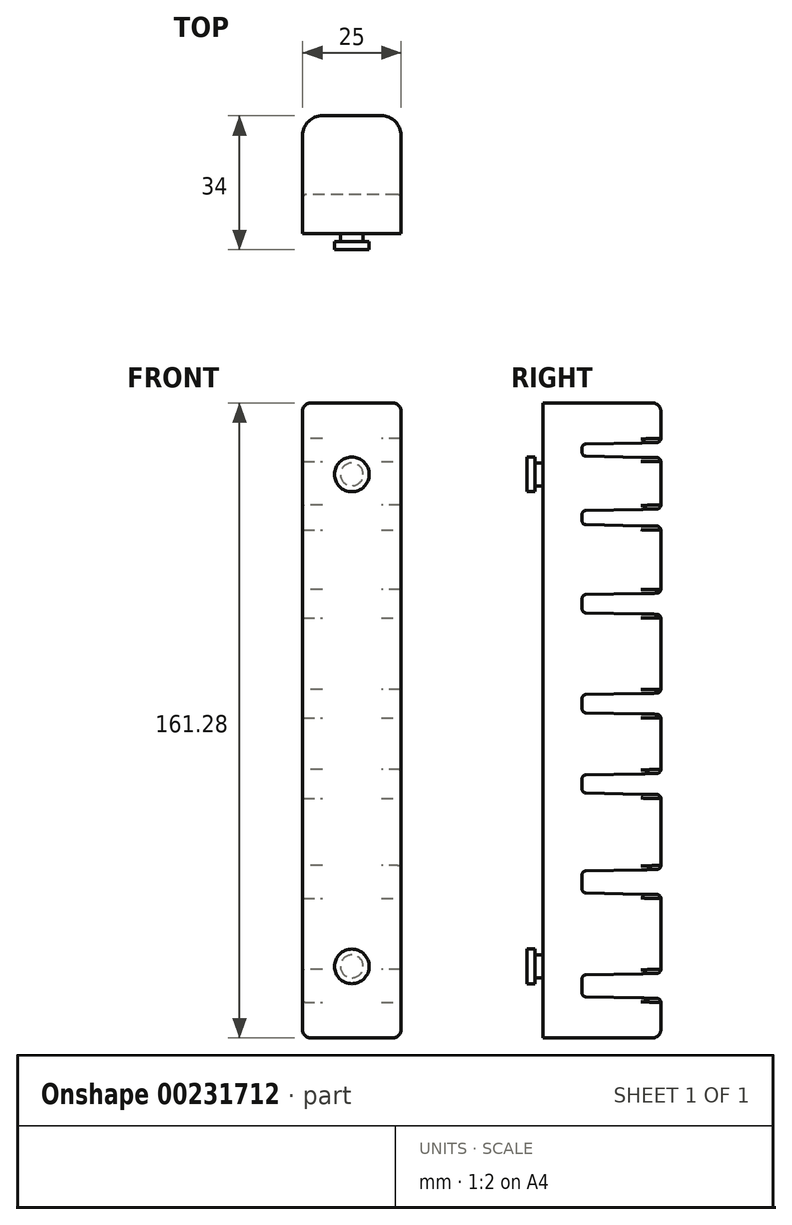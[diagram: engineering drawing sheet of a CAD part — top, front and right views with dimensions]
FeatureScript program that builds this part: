
annotation { "Feature Type Name" : "Feature", "Feature Type Description" : "" }
export const myFeature = defineFeature(function(context is Context, id is Id, definition is map)
    precondition{}
    {
        {
            var Q0;
            Q0=qCreatedBy(makeId("Right.planeOp"),FACE);
            var sketch = newSketch(context, id + "F0", { "sketchPlane" : qUnion([Q0])});
            skLineSegment(sketch, "E0", {"start": v(0, 16.4) * mm, "end": v(-20, 16) * mm});
            skLineSegment(sketch, "E1", {"start": v(-20, 16) * mm, "end": v(-20, 10.4) * mm});
            skLineSegment(sketch, "E2", {"start": v(-20, 10.4) * mm, "end": v(0, 10) * mm});
            skLineSegment(sketch, "E3", {"start": v(-20, 13.2) * mm, "end": v(0, 13.2) * mm, "construction": true});
            skLineSegment(sketch, "E4", {"start": v(-10, 16.2) * mm, "end": v(-9.88, 10.2) * mm, "construction": true});
            skLineSegment(sketch, "E5", {"start": v(0, 42.8) * mm, "end": v(-20, 42.4) * mm});
            skLineSegment(sketch, "E6", {"start": v(-20, 42.4) * mm, "end": v(-20, 36.8) * mm});
            skLineSegment(sketch, "E7", {"start": v(-20, 36.8) * mm, "end": v(0, 36.4) * mm});
            skLineSegment(sketch, "E8", {"start": v(-20, 39.6) * mm, "end": v(0, 39.6) * mm, "construction": true});
            skLineSegment(sketch, "E9", {"start": v(-10, 42.6) * mm, "end": v(-9.88, 36.6) * mm, "construction": true});
            skLineSegment(sketch, "E10", {"start": v(0, 67.19) * mm, "end": v(-20, 66.79) * mm});
            skLineSegment(sketch, "E11", {"start": v(-20, 66.79) * mm, "end": v(-20, 62.2) * mm});
            skLineSegment(sketch, "E12", {"start": v(-20, 62.2) * mm, "end": v(0, 61.8) * mm});
            skLineSegment(sketch, "E13", {"start": v(-20, 64.5) * mm, "end": v(0, 64.5) * mm, "construction": true});
            skLineSegment(sketch, "E14", {"start": v(-10, 66.99) * mm, "end": v(-9.9, 62) * mm, "construction": true});
            skLineSegment(sketch, "E15", {"start": v(0, 87.59) * mm, "end": v(-20, 87.19) * mm});
            skLineSegment(sketch, "E16", {"start": v(-20, 87.19) * mm, "end": v(-20, 82.59) * mm});
            skLineSegment(sketch, "E17", {"start": v(-20, 82.59) * mm, "end": v(0, 82.19) * mm});
            skLineSegment(sketch, "E18", {"start": v(-20, 84.89) * mm, "end": v(0, 84.89) * mm, "construction": true});
            skLineSegment(sketch, "E19", {"start": v(-10, 87.39) * mm, "end": v(-9.9, 82.39) * mm, "construction": true});
            skLineSegment(sketch, "E20", {"start": v(0, 112.98) * mm, "end": v(-20, 112.58) * mm});
            skLineSegment(sketch, "E21", {"start": v(-20, 112.58) * mm, "end": v(-20, 107.99) * mm});
            skLineSegment(sketch, "E22", {"start": v(-20, 107.99) * mm, "end": v(0, 107.59) * mm});
            skLineSegment(sketch, "E23", {"start": v(-20, 110.29) * mm, "end": v(0, 110.29) * mm, "construction": true});
            skLineSegment(sketch, "E24", {"start": v(-10, 112.78) * mm, "end": v(-9.9, 107.78) * mm, "construction": true});
            skLineSegment(sketch, "E25", {"start": v(0, 134.38) * mm, "end": v(-20, 133.98) * mm});
            skLineSegment(sketch, "E26", {"start": v(-20, 133.98) * mm, "end": v(-20, 130.38) * mm});
            skLineSegment(sketch, "E27", {"start": v(-20, 130.38) * mm, "end": v(0, 129.98) * mm});
            skLineSegment(sketch, "E28", {"start": v(-20, 132.18) * mm, "end": v(0, 132.18) * mm, "construction": true});
            skLineSegment(sketch, "E29", {"start": v(-10, 134.18) * mm, "end": v(-9.92, 130.18) * mm, "construction": true});
            skLineSegment(sketch, "E30", {"start": v(0, 151.28) * mm, "end": v(-20, 150.88) * mm});
            skLineSegment(sketch, "E31", {"start": v(-20, 150.88) * mm, "end": v(-20, 147.78) * mm});
            skLineSegment(sketch, "E32", {"start": v(-20, 147.78) * mm, "end": v(0, 147.38) * mm});
            skLineSegment(sketch, "E33", {"start": v(-20, 149.33) * mm, "end": v(0, 149.33) * mm, "construction": true});
            skLineSegment(sketch, "E34", {"start": v(-10, 151.08) * mm, "end": v(-9.93, 147.58) * mm, "construction": true});
            skLineSegment(sketch, "E35", {"start": v(-30, 0) * mm, "end": v(0, 0) * mm});
            skLineSegment(sketch, "E36", {"start": v(0, 0) * mm, "end": v(0, 10) * mm});
            skLineSegment(sketch, "E37", {"start": v(0, 16.4) * mm, "end": v(0, 36.4) * mm});
            skLineSegment(sketch, "E38", {"start": v(0, 42.8) * mm, "end": v(0, 61.8) * mm});
            skLineSegment(sketch, "E39", {"start": v(0, 67.19) * mm, "end": v(0, 82.19) * mm});
            skLineSegment(sketch, "E40", {"start": v(0, 87.59) * mm, "end": v(0, 107.59) * mm});
            skLineSegment(sketch, "E41", {"start": v(0, 112.98) * mm, "end": v(0, 129.98) * mm});
            skLineSegment(sketch, "E42", {"start": v(0, 134.38) * mm, "end": v(0, 147.38) * mm});
            skLineSegment(sketch, "E43", {"start": v(0, 161.28) * mm, "end": v(-30, 161.28) * mm});
            skLineSegment(sketch, "E44", {"start": v(-30, 161.28) * mm, "end": v(-30, 0) * mm});
            skLineSegment(sketch, "E45", {"start": v(0, 151.28) * mm, "end": v(0, 161.28) * mm});
            skSolve(sketch);
        }
        {
            var Q0;
            Q0=makeQuery(id+"F0.imprint","IMPRINT",FACE,{"disambiguationData":[TD([[makeQuery(id+"F0.imprint","IMPRINT",EDGE,{"derivedFrom":sQuery(id+"F0.wireOp",EDGE,"E0")}),-1.0]])]});
            extrude(context, id + "F1", {"entities" : qUnion([Q0]), "depth" : 25 * mm});
        }
        {
            var Q0;
            Q0=makeQuery(id+"F1.opExtrude","SWEPT_FACE",FACE,{"disambiguationData":[OSD([sQuery(id+"F0.wireOp",EDGE,"E44")])]});
            var sketch = newSketch(context, id + "F2", { "sketchPlane" : qUnion([Q0])});
            skLineSegment(sketch, "E46", {"start": v(12.5, 161.28) * mm, "end": v(12.5, 0) * mm, "construction": true});
            skCircle(sketch, "E47", {"center": v(12.5, 143.14) * mm, "radius": 2.9 * mm});
            skCircle(sketch, "E48", {"center": v(12.5, 18.14) * mm, "radius": 2.9 * mm});
            skLineSegment(sketch, "E49", {"start": v(25, 80.64) * mm, "end": v(0, 80.64) * mm, "construction": true});
            skSolve(sketch);
        }
        {
            var Q0;
            Q0 = qSketchRegion(id + "F2", true);
            extrude(context, id + "F3", {"entities" : qUnion([Q0]), "operationType" : NewBodyOperationType.ADD, "depth" : 2 * mm});
        }
        {
            var Q0;
            Q0=makeQuery(id+"F3.opExtrude","CAP_FACE",FACE,{"disambiguationData":[OSD([sQuery(id+"F2.wireOp",EDGE,"E47")])],"isStart":false});
            var sketch = newSketch(context, id + "F4", { "sketchPlane" : qUnion([Q0])});
            skCircle(sketch, "E50.0", {"center": v(12.5, 18.14) * mm, "radius": 2.9 * mm, "construction": true});
            skCircle(sketch, "E51", {"center": v(12.5, 143.14) * mm, "radius": 4.4 * mm});
            skCircle(sketch, "E52", {"center": v(12.5, 18.14) * mm, "radius": 4.4 * mm});
            skSolve(sketch);
        }
        {
            var Q0;
            Q0 = qSketchRegion(id + "F4", true);
            extrude(context, id + "F5", {"entities" : qUnion([Q0]), "operationType" : NewBodyOperationType.ADD, "depth" : 2 * mm});
        }
        {
            var Q0;
            Q0=makeQuery(id+"F1.opExtrude","CAP_EDGE",EDGE,{"disambiguationData":[OSD([sQuery(id+"F0.wireOp",EDGE,"mjwVNYeS-vEzB-6sEj-ztII-VVEKspzb1g9s")])],"isStart":false});
            var Q1;
            Q1=makeQuery(id+"F1.opExtrude","CAP_EDGE",EDGE,{"disambiguationData":[OSD([sQuery(id+"F0.wireOp",EDGE,"kygyZzvb-Qq0e-WmFi-jhyr-vDQcLCwvkyLP")])],"isStart":false});
            var Q2;
            Q2=makeQuery(id+"F1.opExtrude","CAP_EDGE",EDGE,{"disambiguationData":[OSD([sQuery(id+"F0.wireOp",EDGE,"E42")])],"isStart":false});
            var Q3;
            Q3=makeQuery(id+"F1.opExtrude","CAP_EDGE",EDGE,{"disambiguationData":[OSD([sQuery(id+"F0.wireOp",EDGE,"E41")])],"isStart":false});
            var Q4;
            Q4=makeQuery(id+"F1.opExtrude","CAP_EDGE",EDGE,{"disambiguationData":[OSD([sQuery(id+"F0.wireOp",EDGE,"E40")])],"isStart":false});
            var Q5;
            Q5=makeQuery(id+"F1.opExtrude","CAP_EDGE",EDGE,{"disambiguationData":[OSD([sQuery(id+"F0.wireOp",EDGE,"E39")])],"isStart":false});
            var Q6;
            Q6=makeQuery(id+"F1.opExtrude","CAP_EDGE",EDGE,{"disambiguationData":[OSD([sQuery(id+"F0.wireOp",EDGE,"E38")])],"isStart":false});
            var Q7;
            Q7=makeQuery(id+"F1.opExtrude","CAP_EDGE",EDGE,{"disambiguationData":[OSD([sQuery(id+"F0.wireOp",EDGE,"E37")])],"isStart":false});
            var Q8;
            Q8=makeQuery(id+"F1.opExtrude","CAP_EDGE",EDGE,{"disambiguationData":[OSD([sQuery(id+"F0.wireOp",EDGE,"E36")])],"isStart":false});
            var Q9;
            Q9=makeQuery(id+"F1.opExtrude","CAP_EDGE",EDGE,{"disambiguationData":[OSD([sQuery(id+"F0.wireOp",EDGE,"mjwVNYeS-vEzB-6sEj-ztII-VVEKspzb1g9s")])],"isStart":true});
            var Q10;
            Q10=makeQuery(id+"F1.opExtrude","CAP_EDGE",EDGE,{"disambiguationData":[OSD([sQuery(id+"F0.wireOp",EDGE,"kygyZzvb-Qq0e-WmFi-jhyr-vDQcLCwvkyLP")])],"isStart":true});
            var Q11;
            Q11=makeQuery(id+"F1.opExtrude","CAP_EDGE",EDGE,{"disambiguationData":[OSD([sQuery(id+"F0.wireOp",EDGE,"E42")])],"isStart":true});
            var Q12;
            Q12=makeQuery(id+"F1.opExtrude","CAP_EDGE",EDGE,{"disambiguationData":[OSD([sQuery(id+"F0.wireOp",EDGE,"E41")])],"isStart":true});
            var Q13;
            Q13=makeQuery(id+"F1.opExtrude","CAP_EDGE",EDGE,{"disambiguationData":[OSD([sQuery(id+"F0.wireOp",EDGE,"E40")])],"isStart":true});
            var Q14;
            Q14=makeQuery(id+"F1.opExtrude","CAP_EDGE",EDGE,{"disambiguationData":[OSD([sQuery(id+"F0.wireOp",EDGE,"E39")])],"isStart":true});
            var Q15;
            Q15=makeQuery(id+"F1.opExtrude","CAP_EDGE",EDGE,{"disambiguationData":[OSD([sQuery(id+"F0.wireOp",EDGE,"E38")])],"isStart":true});
            var Q16;
            Q16=makeQuery(id+"F1.opExtrude","CAP_EDGE",EDGE,{"disambiguationData":[OSD([sQuery(id+"F0.wireOp",EDGE,"E37")])],"isStart":true});
            var Q17;
            Q17=makeQuery(id+"F1.opExtrude","CAP_EDGE",EDGE,{"disambiguationData":[OSD([sQuery(id+"F0.wireOp",EDGE,"E36")])],"isStart":true});
            var Q18;
            Q18=makeQuery(id+"F1.opExtrude","CAP_EDGE",EDGE,{"disambiguationData":[OSD([sQuery(id+"F0.wireOp",EDGE,"E45")])],"isStart":false});
            var Q19;
            Q19=makeQuery(id+"F1.opExtrude","CAP_EDGE",EDGE,{"disambiguationData":[OSD([sQuery(id+"F0.wireOp",EDGE,"E45")])],"isStart":true});
            fillet(context, id + "F6", {"entities" : qUnion([Q0, Q1, Q2, Q3, Q4, Q5, Q6, Q7, Q8, Q9, Q10, Q11, Q12, Q13, Q14, Q15, Q16, Q17, Q18, Q19]), "radius" : 5 * mm, "tangentPropagation" : true, "allowEdgeOverflow" : false});
        }
        {
            var Q0;
            Q0=makeQuery(id+"F1.opExtrude","CAP_EDGE",EDGE,{"disambiguationData":[OSD([sQuery(id+"F0.wireOp",EDGE,"E43")])],"isStart":false});
            var Q1;
            Q1=makeQuery(id+"F1.opExtrude","CAP_EDGE",EDGE,{"disambiguationData":[OSD([sQuery(id+"F0.wireOp",EDGE,"E35")])],"isStart":false});
            fillet(context, id + "F7", {"entities" : qUnion([Q0, Q1]), "radius" : 2 * mm, "tangentPropagation" : true, "allowEdgeOverflow" : false});
        }
        {
            var Q0;
            Q0=makeQuery(id+"F1.opExtrude","SWEPT_EDGE",EDGE,{"disambiguationData":[OSD([sQuery(id+"F0.wireOp",EDGE,"E0"),sQuery(id+"F0.wireOp",EDGE,"E1")])]});
            var Q1;
            Q1=makeQuery(id+"F1.opExtrude","SWEPT_EDGE",EDGE,{"disambiguationData":[OSD([sQuery(id+"F0.wireOp",EDGE,"E5"),sQuery(id+"F0.wireOp",EDGE,"E6")])]});
            var Q2;
            Q2=makeQuery(id+"F1.opExtrude","SWEPT_EDGE",EDGE,{"disambiguationData":[OSD([sQuery(id+"F0.wireOp",EDGE,"E10"),sQuery(id+"F0.wireOp",EDGE,"E11")])]});
            var Q3;
            Q3=makeQuery(id+"F1.opExtrude","SWEPT_EDGE",EDGE,{"disambiguationData":[OSD([sQuery(id+"F0.wireOp",EDGE,"E15"),sQuery(id+"F0.wireOp",EDGE,"E16")])]});
            var Q4;
            Q4=makeQuery(id+"F1.opExtrude","SWEPT_EDGE",EDGE,{"disambiguationData":[OSD([sQuery(id+"F0.wireOp",EDGE,"E20"),sQuery(id+"F0.wireOp",EDGE,"E21")])]});
            var Q5;
            Q5=makeQuery(id+"F1.opExtrude","SWEPT_EDGE",EDGE,{"disambiguationData":[OSD([sQuery(id+"F0.wireOp",EDGE,"E25"),sQuery(id+"F0.wireOp",EDGE,"E26")])]});
            var Q6;
            Q6=makeQuery(id+"F1.opExtrude","SWEPT_EDGE",EDGE,{"disambiguationData":[OSD([sQuery(id+"F0.wireOp",EDGE,"E30"),sQuery(id+"F0.wireOp",EDGE,"E31")])]});
            var Q7;
            Q7=makeQuery(id+"F1.opExtrude","SWEPT_EDGE",EDGE,{"disambiguationData":[OSD([sQuery(id+"F0.wireOp",EDGE,"04d1fc47-b4e6-4801-867b-3d0f7dd9d733"),sQuery(id+"F0.wireOp",EDGE,"0a8521f6-aab2-45d8-91f2-bb453d14134b")])]});
            var Q8;
            Q8=makeQuery(id+"F1.opExtrude","SWEPT_EDGE",EDGE,{"disambiguationData":[OSD([sQuery(id+"F0.wireOp",EDGE,"E1"),sQuery(id+"F0.wireOp",EDGE,"E2")])]});
            var Q9;
            Q9=makeQuery(id+"F1.opExtrude","SWEPT_EDGE",EDGE,{"disambiguationData":[OSD([sQuery(id+"F0.wireOp",EDGE,"E6"),sQuery(id+"F0.wireOp",EDGE,"E7")])]});
            var Q10;
            Q10=makeQuery(id+"F1.opExtrude","SWEPT_EDGE",EDGE,{"disambiguationData":[OSD([sQuery(id+"F0.wireOp",EDGE,"E11"),sQuery(id+"F0.wireOp",EDGE,"E12")])]});
            var Q11;
            Q11=makeQuery(id+"F1.opExtrude","SWEPT_EDGE",EDGE,{"disambiguationData":[OSD([sQuery(id+"F0.wireOp",EDGE,"E16"),sQuery(id+"F0.wireOp",EDGE,"E17")])]});
            var Q12;
            Q12=makeQuery(id+"F1.opExtrude","SWEPT_EDGE",EDGE,{"disambiguationData":[OSD([sQuery(id+"F0.wireOp",EDGE,"E21"),sQuery(id+"F0.wireOp",EDGE,"E22")])]});
            var Q13;
            Q13=makeQuery(id+"F1.opExtrude","SWEPT_EDGE",EDGE,{"disambiguationData":[OSD([sQuery(id+"F0.wireOp",EDGE,"E26"),sQuery(id+"F0.wireOp",EDGE,"E27")])]});
            var Q14;
            Q14=makeQuery(id+"F1.opExtrude","SWEPT_EDGE",EDGE,{"disambiguationData":[OSD([sQuery(id+"F0.wireOp",EDGE,"E31"),sQuery(id+"F0.wireOp",EDGE,"E32")])]});
            var Q15;
            Q15=makeQuery(id+"F1.opExtrude","SWEPT_EDGE",EDGE,{"disambiguationData":[OSD([sQuery(id+"F0.wireOp",EDGE,"0a8521f6-aab2-45d8-91f2-bb453d14134b"),sQuery(id+"F0.wireOp",EDGE,"10080821-f725-45bf-a71c-607c7a7e03e2")])]});
            fillet(context, id + "F8", {"entities" : qUnion([Q0, Q1, Q2, Q3, Q4, Q5, Q6, Q7, Q8, Q9, Q10, Q11, Q12, Q13, Q14, Q15]), "radius" : 1 * mm, "tangentPropagation" : true, "allowEdgeOverflow" : false});
        }
        {
            var Q0;
            Q0=makeQuery(id+"F1.opExtrude","CAP_EDGE",EDGE,{"disambiguationData":[OSD([sQuery(id+"F0.wireOp",EDGE,"10080821-f725-45bf-a71c-607c7a7e03e2")])],"isStart":false});
            var Q1;
            Q1=makeQuery(id+"F1.opExtrude","CAP_EDGE",EDGE,{"disambiguationData":[OSD([sQuery(id+"F0.wireOp",EDGE,"E32")])],"isStart":false});
            var Q2;
            Q2=makeQuery(id+"F1.opExtrude","CAP_EDGE",EDGE,{"disambiguationData":[OSD([sQuery(id+"F0.wireOp",EDGE,"E27")])],"isStart":false});
            var Q3;
            Q3=makeQuery(id+"F1.opExtrude","CAP_EDGE",EDGE,{"disambiguationData":[OSD([sQuery(id+"F0.wireOp",EDGE,"E22")])],"isStart":false});
            var Q4;
            Q4=makeQuery(id+"F1.opExtrude","CAP_EDGE",EDGE,{"disambiguationData":[OSD([sQuery(id+"F0.wireOp",EDGE,"E17")])],"isStart":false});
            var Q5;
            Q5=makeQuery(id+"F1.opExtrude","CAP_EDGE",EDGE,{"disambiguationData":[OSD([sQuery(id+"F0.wireOp",EDGE,"E12")])],"isStart":false});
            var Q6;
            Q6=makeQuery(id+"F1.opExtrude","CAP_EDGE",EDGE,{"disambiguationData":[OSD([sQuery(id+"F0.wireOp",EDGE,"E7")])],"isStart":false});
            var Q7;
            Q7=makeQuery(id+"F1.opExtrude","CAP_EDGE",EDGE,{"disambiguationData":[OSD([sQuery(id+"F0.wireOp",EDGE,"E2")])],"isStart":false});
            fillet(context, id + "F9", {"entities" : qUnion([Q0, Q1, Q2, Q3, Q4, Q5, Q6, Q7]), "radius" : 1 * mm, "tangentPropagation" : true, "allowEdgeOverflow" : false});
        }
    });
